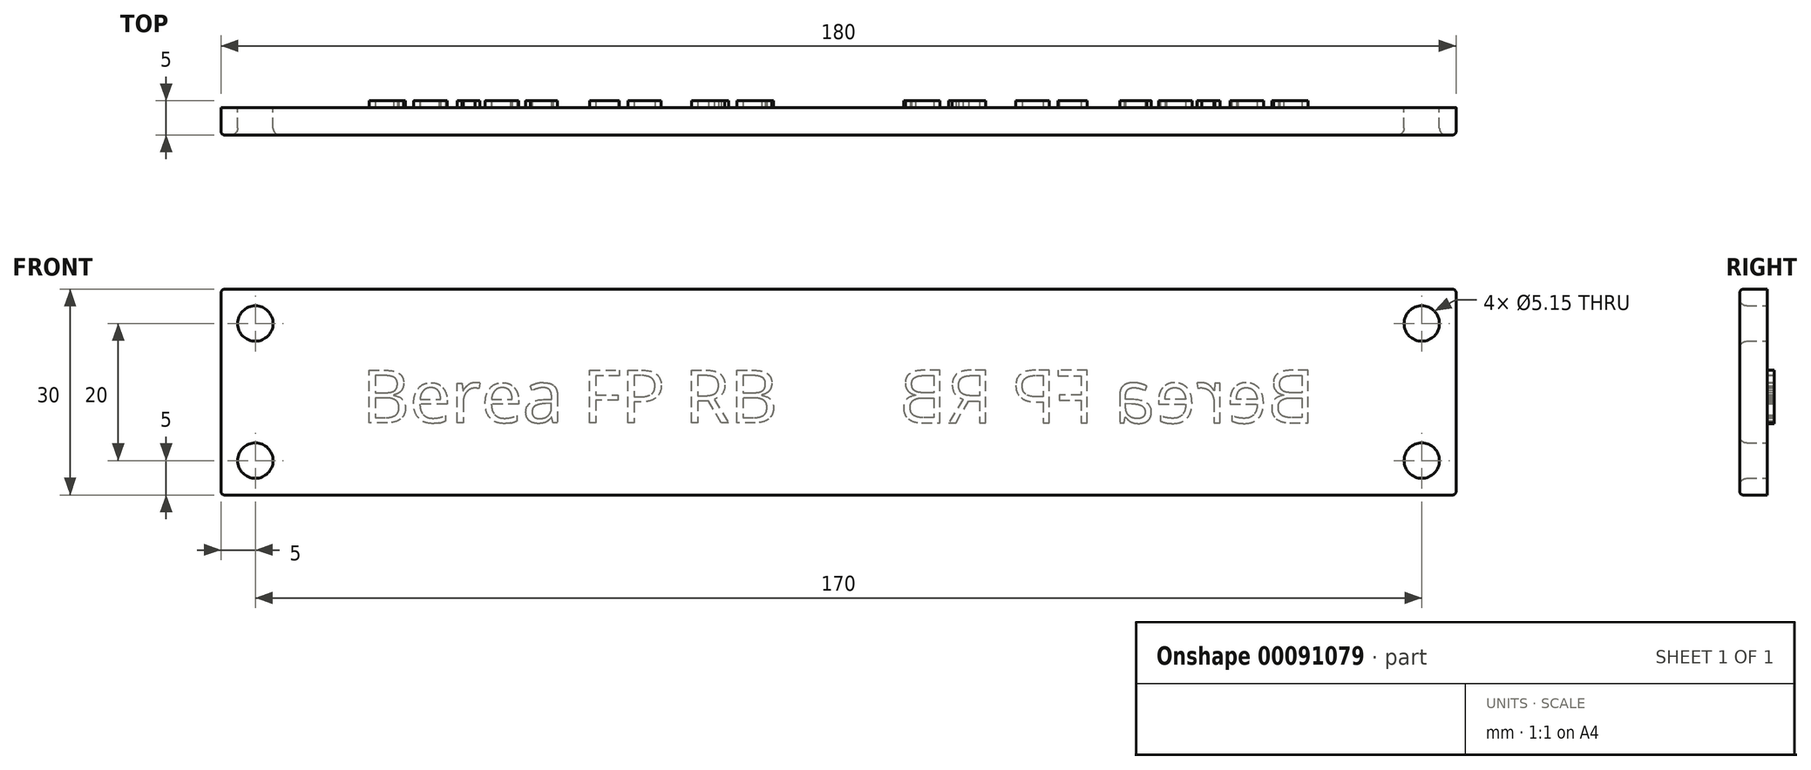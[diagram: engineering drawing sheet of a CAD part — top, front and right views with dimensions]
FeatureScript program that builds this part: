
annotation { "Feature Type Name" : "Feature", "Feature Type Description" : "" }
export const myFeature = defineFeature(function(context is Context, id is Id, definition is map)
    precondition{}
    {
        {
            var Q0;
            Q0=qCreatedBy(makeId("Front.planeOp"),FACE);
            var sketch = newSketch(context, id + "F0", { "sketchPlane" : qUnion([Q0])});
            skLineSegment(sketch, "E0.bottom", {"start": v(-90, -15) * mm, "end": v(90, -15) * mm});
            skLineSegment(sketch, "E0.top", {"start": v(-90, 15) * mm, "end": v(90, 15) * mm});
            skLineSegment(sketch, "E0.left", {"start": v(-90, -15) * mm, "end": v(-90, 15) * mm});
            skLineSegment(sketch, "E0.right", {"start": v(90, -15) * mm, "end": v(90, 15) * mm});
            skPoint(sketch, "E0.middle", {"position": v(0, 0) * mm});
            skCircle(sketch, "E1", {"center": v(-85, 10) * mm, "radius": 2.58 * mm});
            skPoint(sketch, "E2.start.orphan", {"position": v(-90, 0) * mm});
            skPoint(sketch, "E3.orphan", {"position": v(0, 15) * mm});
            skPoint(sketch, "E4.end.orphan", {"position": v(0, -15) * mm});
            skLineSegment(sketch, "E5", {"start": v(-90, 0) * mm, "end": v(0, 0) * mm, "construction": true});
            skLineSegment(sketch, "E6", {"start": v(0, 15) * mm, "end": v(0, -15) * mm, "construction": true});
            skCircle(sketch, "E7.MirrorC", {"center": v(-85, -10) * mm, "radius": 2.58 * mm});
            skCircle(sketch, "E8.MirrorC", {"center": v(85, 10) * mm, "radius": 2.58 * mm});
            skCircle(sketch, "E9.MirrorC", {"center": v(85, -10) * mm, "radius": 2.58 * mm});
            skSolve(sketch);
        }
        {
            var Q0;
            Q0=makeQuery(id+"F0.imprint","IMPRINT",FACE,{"disambiguationData":[TD([[makeQuery(id+"F0.imprint","IMPRINT",EDGE,{"derivedFrom":sQuery(id+"F0.wireOp",EDGE,"E0.bottom")}),1.0]])]});
            extrude(context, id + "F1", {"entities" : qUnion([Q0]), "depth" : 4 * mm});
        }
        {
            var Q0;
            Q0=makeQuery(id+"F1.opExtrude","CAP_EDGE",EDGE,{"disambiguationData":[OSD([sQuery(id+"F0.wireOp",EDGE,"E1")])],"isStart":false});
            var Q1;
            Q1=makeQuery(id+"F1.opExtrude","CAP_EDGE",EDGE,{"disambiguationData":[OSD([sQuery(id+"F0.wireOp",EDGE,"f5b72a5b-8583-449a-bdbf-9ac5a681e1fd0.MirrorC")])],"isStart":false});
            var Q2;
            Q2=makeQuery(id+"F1.opExtrude","CAP_EDGE",EDGE,{"disambiguationData":[OSD([sQuery(id+"F0.wireOp",EDGE,"2623e306-60f4-4522-aa65-1e3e8c2cf5b60.MirrorC")])],"isStart":false});
            var Q3;
            Q3=makeQuery(id+"F1.opExtrude","CAP_EDGE",EDGE,{"disambiguationData":[OSD([sQuery(id+"F0.wireOp",EDGE,"be81a34d-1d50-4ce7-a7a8-4484a1701fac0.MirrorC")])],"isStart":false});
            var Q4;
            Q4=makeQuery(id+"F1.opExtrude","CAP_EDGE",EDGE,{"disambiguationData":[OSD([sQuery(id+"F0.wireOp",EDGE,"E7.MirrorC")])],"isStart":false});
            var Q5;
            Q5=makeQuery(id+"F1.opExtrude","CAP_EDGE",EDGE,{"disambiguationData":[OSD([sQuery(id+"F0.wireOp",EDGE,"E8.MirrorC")])],"isStart":false});
            var Q6;
            Q6=makeQuery(id+"F1.opExtrude","CAP_EDGE",EDGE,{"disambiguationData":[OSD([sQuery(id+"F0.wireOp",EDGE,"E9.MirrorC")])],"isStart":false});
            fillet(context, id + "F2", {"entities" : qUnion([Q0, Q1, Q2, Q3, Q4, Q5, Q6]), "radius" : 1 * mm, "tangentPropagation" : true, "allowEdgeOverflow" : false});
        }
        {
            var Q0;
            Q0=makeQuery(id+"F1.opExtrude","CAP_EDGE",EDGE,{"disambiguationData":[OSD([sQuery(id+"F0.wireOp",EDGE,"E0.top")])],"isStart":false});
            var Q1;
            Q1=makeQuery(id+"F1.opExtrude","CAP_EDGE",EDGE,{"disambiguationData":[OSD([sQuery(id+"F0.wireOp",EDGE,"E0.left")])],"isStart":false});
            var Q2;
            Q2=makeQuery(id+"F1.opExtrude","CAP_EDGE",EDGE,{"disambiguationData":[OSD([sQuery(id+"F0.wireOp",EDGE,"E0.bottom")])],"isStart":false});
            var Q3;
            Q3=makeQuery(id+"F1.opExtrude","CAP_EDGE",EDGE,{"disambiguationData":[OSD([sQuery(id+"F0.wireOp",EDGE,"E0.right")])],"isStart":false});
            var Q4;
            Q4=makeQuery(id+"F1.opExtrude","SWEPT_EDGE",EDGE,{"disambiguationData":[OSD([sQuery(id+"F0.wireOp",EDGE,"E0.top"),sQuery(id+"F0.wireOp",EDGE,"E0.left")])]});
            var Q5;
            Q5=makeQuery(id+"F1.opExtrude","SWEPT_EDGE",EDGE,{"disambiguationData":[OSD([sQuery(id+"F0.wireOp",EDGE,"E0.bottom"),sQuery(id+"F0.wireOp",EDGE,"E0.left")])]});
            var Q6;
            Q6=makeQuery(id+"F1.opExtrude","SWEPT_EDGE",EDGE,{"disambiguationData":[OSD([sQuery(id+"F0.wireOp",EDGE,"E0.top"),sQuery(id+"F0.wireOp",EDGE,"E0.right")])]});
            var Q7;
            Q7=makeQuery(id+"F1.opExtrude","SWEPT_EDGE",EDGE,{"disambiguationData":[OSD([sQuery(id+"F0.wireOp",EDGE,"E0.bottom"),sQuery(id+"F0.wireOp",EDGE,"E0.right")])]});
            fillet(context, id + "F3", {"entities" : qUnion([Q0, Q1, Q2, Q3, Q4, Q5, Q6, Q7]), "radius" : .5 * mm, "tangentPropagation" : true, "allowEdgeOverflow" : false});
        }
        {
            var Q0;
            Q0=makeQuery(id+"F1.opExtrude","CAP_FACE",FACE,{"disambiguationData":[OSD([sQuery(id+"F0.wireOp",EDGE,"E0.bottom"),sQuery(id+"F0.wireOp",EDGE,"E0.top"),sQuery(id+"F0.wireOp",EDGE,"E0.left"),sQuery(id+"F0.wireOp",EDGE,"E0.right"),sQuery(id+"F0.wireOp",EDGE,"E1"),sQuery(id+"F0.wireOp",EDGE,"E7.MirrorC"),sQuery(id+"F0.wireOp",EDGE,"E8.MirrorC"),sQuery(id+"F0.wireOp",EDGE,"E9.MirrorC")])],"isStart":true});
            var sketch = newSketch(context, id + "F4", { "sketchPlane" : qUnion([Q0])});
            skText(sketch, "E10", { "text": "Berea FP RB", "fontName": "OpenSans-Regular.ttf"});
            skLineSegment(sketch, "E11", {"start": v(0, 15) * mm, "end": v(0, -15) * mm, "construction": true});
            const initialGuessF4  = {"E10": [-0.0695, -0.00448, 1, 0, 0.00774]};
            skSetInitialGuess(sketch, initialGuessF4);
            skSolve(sketch);
        }
        {
            var Q0;
            Q0=qSketchRegion(id+"F4",true);
            extrude(context, id + "F5", {"entities" : qUnion([Q0]), "operationType" : NewBodyOperationType.ADD, "depth" : 1 * mm});
        }
        {
            var Q0;
            Q0=makeQuery(id+"F1.opExtrude","SWEPT_BODY",BODY,{"disambiguationData":[OSD([sQuery(id+"F0.wireOp",EDGE,"E0.bottom"),sQuery(id+"F0.wireOp",EDGE,"E0.top"),sQuery(id+"F0.wireOp",EDGE,"E0.left"),sQuery(id+"F0.wireOp",EDGE,"E0.right"),sQuery(id+"F0.wireOp",EDGE,"E1"),sQuery(id+"F0.wireOp",EDGE,"E7.MirrorC"),sQuery(id+"F0.wireOp",EDGE,"E8.MirrorC"),sQuery(id+"F0.wireOp",EDGE,"E9.MirrorC")])]});
            var Q1;
            Q1=makeQuery(id+"F5.opExtrude","SWEPT_FACE",FACE,{"disambiguationData":[OSD([sQuery(id+"F4.wireOp",EDGE,"E10.sketch_text.stroke-94")])]});
            var Q2;
            Q2=makeQuery(id+"F5.opExtrude","SWEPT_FACE",FACE,{"disambiguationData":[OSD([sQuery(id+"F4.wireOp",EDGE,"E10.sketch_text.stroke-169")])]});
            var Q3;
            Q3=makeQuery(id+"F5.opExtrude","SWEPT_FACE",FACE,{"disambiguationData":[OSD([sQuery(id+"F4.wireOp",EDGE,"E10.sketch_text.stroke-185")])]});
            var Q4;
            Q4=makeQuery(id+"F5.opExtrude","SWEPT_FACE",FACE,{"disambiguationData":[OSD([sQuery(id+"F4.wireOp",EDGE,"E10.sketch_text.stroke-125")])]});
            var Q5;
            Q5=makeQuery(id+"F5.opExtrude","SWEPT_FACE",FACE,{"disambiguationData":[OSD([sQuery(id+"F4.wireOp",EDGE,"E10.sketch_text.stroke-155")])]});
            var Q6;
            Q6=makeQuery(id+"F5.opExtrude","SWEPT_FACE",FACE,{"disambiguationData":[OSD([sQuery(id+"F4.wireOp",EDGE,"E10.sketch_text.stroke-65")])]});
            var Q7;
            Q7=makeQuery(id+"F5.opExtrude","SWEPT_FACE",FACE,{"disambiguationData":[OSD([sQuery(id+"F4.wireOp",EDGE,"E10.sketch_text.stroke-81")])]});
            var Q8;
            Q8=makeQuery(id+"F5.opExtrude","SWEPT_FACE",FACE,{"disambiguationData":[OSD([sQuery(id+"F4.wireOp",EDGE,"E10.sketch_text.stroke-67")])]});
            var Q9;
            Q9=makeQuery(id+"F5.opExtrude","SWEPT_FACE",FACE,{"disambiguationData":[OSD([sQuery(id+"F4.wireOp",EDGE,"E10.sketch_text.stroke-99")])]});
            var Q10;
            Q10=makeQuery(id+"F5.opExtrude","SWEPT_FACE",FACE,{"disambiguationData":[OSD([sQuery(id+"F4.wireOp",EDGE,"E10.sketch_text.stroke-127")])]});
            var Q11;
            Q11=makeQuery(id+"F5.opExtrude","SWEPT_FACE",FACE,{"disambiguationData":[OSD([sQuery(id+"F4.wireOp",EDGE,"E10.sketch_text.stroke-10")])]});
            var Q12;
            Q12=makeQuery(id+"F5.opExtrude","CAP_FACE",FACE,{"disambiguationData":[OSD([sQuery(id+"F4.wireOp",EDGE,"E10.sketch_text.stroke-9"),sQuery(id+"F4.wireOp",EDGE,"E10.sketch_text.stroke-10"),sQuery(id+"F4.wireOp",EDGE,"E10.sketch_text.stroke-11"),sQuery(id+"F4.wireOp",EDGE,"E10.sketch_text.stroke-12")])],"isStart":false});
            var Q13;
            Q13=makeQuery(id+"F5.opExtrude","SWEPT_FACE",FACE,{"disambiguationData":[OSD([sQuery(id+"F4.wireOp",EDGE,"E10.sketch_text.stroke-154")])]});
            var Q14;
            Q14=makeQuery(id+"F5.opExtrude","SWEPT_FACE",FACE,{"disambiguationData":[OSD([sQuery(id+"F4.wireOp",EDGE,"E10.sketch_text.stroke-1")])]});
            var Q15;
            Q15=makeQuery(id+"F5.opExtrude","CAP_FACE",FACE,{"disambiguationData":[OSD([sQuery(id+"F4.wireOp",EDGE,"E10.sketch_text.stroke-124"),sQuery(id+"F4.wireOp",EDGE,"E10.sketch_text.stroke-125"),sQuery(id+"F4.wireOp",EDGE,"E10.sketch_text.stroke-126"),sQuery(id+"F4.wireOp",EDGE,"E10.sketch_text.stroke-127"),sQuery(id+"F4.wireOp",EDGE,"E10.sketch_text.stroke-128"),sQuery(id+"F4.wireOp",EDGE,"E10.sketch_text.stroke-129"),sQuery(id+"F4.wireOp",EDGE,"E10.sketch_text.stroke-130"),sQuery(id+"F4.wireOp",EDGE,"E10.sketch_text.stroke-131"),sQuery(id+"F4.wireOp",EDGE,"E10.sketch_text.stroke-132"),sQuery(id+"F4.wireOp",EDGE,"E10.sketch_text.stroke-133"),sQuery(id+"F4.wireOp",EDGE,"E10.sketch_text.stroke-134"),sQuery(id+"F4.wireOp",EDGE,"E10.sketch_text.stroke-135"),sQuery(id+"F4.wireOp",EDGE,"E10.sketch_text.stroke-136"),sQuery(id+"F4.wireOp",EDGE,"E10.sketch_text.stroke-137"),sQuery(id+"F4.wireOp",EDGE,"E10.sketch_text.stroke-138")])],"isStart":false});
            var Q16;
            Q16=makeQuery(id+"F5.opExtrude","CAP_FACE",FACE,{"disambiguationData":[OSD([sQuery(id+"F4.wireOp",EDGE,"E10.sketch_text.stroke-34"),sQuery(id+"F4.wireOp",EDGE,"E10.sketch_text.stroke-35"),sQuery(id+"F4.wireOp",EDGE,"E10.sketch_text.stroke-36"),sQuery(id+"F4.wireOp",EDGE,"E10.sketch_text.stroke-37"),sQuery(id+"F4.wireOp",EDGE,"E10.sketch_text.stroke-38"),sQuery(id+"F4.wireOp",EDGE,"E10.sketch_text.stroke-39"),sQuery(id+"F4.wireOp",EDGE,"E10.sketch_text.stroke-40"),sQuery(id+"F4.wireOp",EDGE,"E10.sketch_text.stroke-41"),sQuery(id+"F4.wireOp",EDGE,"E10.sketch_text.stroke-42"),sQuery(id+"F4.wireOp",EDGE,"E10.sketch_text.stroke-43"),sQuery(id+"F4.wireOp",EDGE,"E10.sketch_text.stroke-44"),sQuery(id+"F4.wireOp",EDGE,"E10.sketch_text.stroke-45"),sQuery(id+"F4.wireOp",EDGE,"E10.sketch_text.stroke-46"),sQuery(id+"F4.wireOp",EDGE,"E10.sketch_text.stroke-47"),sQuery(id+"F4.wireOp",EDGE,"E10.sketch_text.stroke-48"),sQuery(id+"F4.wireOp",EDGE,"E10.sketch_text.stroke-49"),sQuery(id+"F4.wireOp",EDGE,"E10.sketch_text.stroke-50"),sQuery(id+"F4.wireOp",EDGE,"E10.sketch_text.stroke-51"),sQuery(id+"F4.wireOp",EDGE,"E10.sketch_text.stroke-52"),sQuery(id+"F4.wireOp",EDGE,"E10.sketch_text.stroke-53"),sQuery(id+"F4.wireOp",EDGE,"E10.sketch_text.stroke-54"),sQuery(id+"F4.wireOp",EDGE,"E10.sketch_text.stroke-55"),sQuery(id+"F4.wireOp",EDGE,"E10.sketch_text.stroke-56"),sQuery(id+"F4.wireOp",EDGE,"E10.sketch_text.stroke-57"),sQuery(id+"F4.wireOp",EDGE,"E10.sketch_text.stroke-58"),sQuery(id+"F4.wireOp",EDGE,"E10.sketch_text.stroke-59"),sQuery(id+"F4.wireOp",EDGE,"E10.sketch_text.stroke-60")])],"isStart":false});
            var Q17;
            Q17=makeQuery(id+"F5.opExtrude","SWEPT_FACE",FACE,{"disambiguationData":[OSD([sQuery(id+"F4.wireOp",EDGE,"E10.sketch_text.stroke-50")])]});
            var Q18;
            Q18=makeQuery(id+"F5.opExtrude","SWEPT_FACE",FACE,{"disambiguationData":[OSD([sQuery(id+"F4.wireOp",EDGE,"E10.sketch_text.stroke-2")])]});
            var Q19;
            Q19=makeQuery(id+"F5.opExtrude","SWEPT_FACE",FACE,{"disambiguationData":[OSD([sQuery(id+"F4.wireOp",EDGE,"E10.sketch_text.stroke-3")])]});
            var Q20;
            Q20=makeQuery(id+"F5.opExtrude","SWEPT_FACE",FACE,{"disambiguationData":[OSD([sQuery(id+"F4.wireOp",EDGE,"E10.sketch_text.stroke-5")])]});
            var Q21;
            Q21=makeQuery(id+"F5.opExtrude","SWEPT_FACE",FACE,{"disambiguationData":[OSD([sQuery(id+"F4.wireOp",EDGE,"E10.sketch_text.stroke-8")])]});
            var Q22;
            Q22=makeQuery(id+"F5.opExtrude","SWEPT_FACE",FACE,{"disambiguationData":[OSD([sQuery(id+"F4.wireOp",EDGE,"E10.sketch_text.stroke-98")])]});
            var Q23;
            Q23=makeQuery(id+"F5.opExtrude","SWEPT_FACE",FACE,{"disambiguationData":[OSD([sQuery(id+"F4.wireOp",EDGE,"E10.sketch_text.stroke-66")])]});
            var Q24;
            Q24=makeQuery(id+"F5.opExtrude","SWEPT_FACE",FACE,{"disambiguationData":[OSD([sQuery(id+"F4.wireOp",EDGE,"E10.sketch_text.stroke-153")])]});
            var Q25;
            Q25=makeQuery(id+"F5.opExtrude","SWEPT_FACE",FACE,{"disambiguationData":[OSD([sQuery(id+"F4.wireOp",EDGE,"E10.sketch_text.stroke-126")])]});
            var Q26;
            Q26=makeQuery(id+"F5.opExtrude","SWEPT_FACE",FACE,{"disambiguationData":[OSD([sQuery(id+"F4.wireOp",EDGE,"E10.sketch_text.stroke-183")])]});
            var Q27;
            Q27=makeQuery(id+"F5.opExtrude","SWEPT_FACE",FACE,{"disambiguationData":[OSD([sQuery(id+"F4.wireOp",EDGE,"E10.sketch_text.stroke-109")])]});
            var Q28;
            Q28=makeQuery(id+"F5.opExtrude","SWEPT_FACE",FACE,{"disambiguationData":[OSD([sQuery(id+"F4.wireOp",EDGE,"E10.sketch_text.stroke-186")])]});
            var Q29;
            Q29=makeQuery(id+"F5.opExtrude","SWEPT_FACE",FACE,{"disambiguationData":[OSD([sQuery(id+"F4.wireOp",EDGE,"E10.sketch_text.stroke-79")])]});
            var Q30;
            Q30=makeQuery(id+"F5.opExtrude","SWEPT_FACE",FACE,{"disambiguationData":[OSD([sQuery(id+"F4.wireOp",EDGE,"E10.sketch_text.stroke-110")])]});
            var Q31;
            Q31=makeQuery(id+"F5.opExtrude","SWEPT_FACE",FACE,{"disambiguationData":[OSD([sQuery(id+"F4.wireOp",EDGE,"E10.sketch_text.stroke-38")])]});
            var Q32;
            Q32=makeQuery(id+"F5.opExtrude","SWEPT_FACE",FACE,{"disambiguationData":[OSD([sQuery(id+"F4.wireOp",EDGE,"E10.sketch_text.stroke-24")])]});
            var Q33;
            Q33=makeQuery(id+"F5.opExtrude","SWEPT_FACE",FACE,{"disambiguationData":[OSD([sQuery(id+"F4.wireOp",EDGE,"E10.sketch_text.stroke-12")])]});
            var Q34;
            Q34=makeQuery(id+"F5.opExtrude","SWEPT_FACE",FACE,{"disambiguationData":[OSD([sQuery(id+"F4.wireOp",EDGE,"E10.sketch_text.stroke-100")])]});
            var Q35;
            Q35=makeQuery(id+"F5.opExtrude","SWEPT_FACE",FACE,{"disambiguationData":[OSD([sQuery(id+"F4.wireOp",EDGE,"E10.sketch_text.stroke-158")])]});
            var Q36;
            Q36=makeQuery(id+"F5.opExtrude","SWEPT_FACE",FACE,{"disambiguationData":[OSD([sQuery(id+"F4.wireOp",EDGE,"E10.sketch_text.stroke-142")])]});
            var Q37;
            Q37=makeQuery(id+"F5.opExtrude","SWEPT_FACE",FACE,{"disambiguationData":[OSD([sQuery(id+"F4.wireOp",EDGE,"E10.sketch_text.stroke-54")])]});
            var Q38;
            Q38=makeQuery(id+"F5.opExtrude","SWEPT_FACE",FACE,{"disambiguationData":[OSD([sQuery(id+"F4.wireOp",EDGE,"E10.sketch_text.stroke-25")])]});
            var Q39;
            Q39=makeQuery(id+"F5.opExtrude","SWEPT_FACE",FACE,{"disambiguationData":[OSD([sQuery(id+"F4.wireOp",EDGE,"E10.sketch_text.stroke-101")])]});
            var Q40;
            Q40=makeQuery(id+"F5.opExtrude","SWEPT_FACE",FACE,{"disambiguationData":[OSD([sQuery(id+"F4.wireOp",EDGE,"E10.sketch_text.stroke-69")])]});
            var Q41;
            Q41=makeQuery(id+"F5.opExtrude","SWEPT_FACE",FACE,{"disambiguationData":[OSD([sQuery(id+"F4.wireOp",EDGE,"E10.sketch_text.stroke-159")])]});
            var Q42;
            Q42=makeQuery(id+"F5.opExtrude","SWEPT_FACE",FACE,{"disambiguationData":[OSD([sQuery(id+"F4.wireOp",EDGE,"E10.sketch_text.stroke-85")])]});
            var Q43;
            Q43=makeQuery(id+"F5.opExtrude","SWEPT_FACE",FACE,{"disambiguationData":[OSD([sQuery(id+"F4.wireOp",EDGE,"E10.sketch_text.stroke-173")])]});
            var Q44;
            Q44=makeQuery(id+"F5.opExtrude","SWEPT_FACE",FACE,{"disambiguationData":[OSD([sQuery(id+"F4.wireOp",EDGE,"E10.sketch_text.stroke-40")])]});
            var Q45;
            Q45=makeQuery(id+"F5.opExtrude","SWEPT_FACE",FACE,{"disambiguationData":[OSD([sQuery(id+"F4.wireOp",EDGE,"E10.sketch_text.stroke-102")])]});
            var Q46;
            Q46=makeQuery(id+"F5.opExtrude","SWEPT_FACE",FACE,{"disambiguationData":[OSD([sQuery(id+"F4.wireOp",EDGE,"E10.sketch_text.stroke-86")])]});
            var Q47;
            Q47=makeQuery(id+"F5.opExtrude","SWEPT_FACE",FACE,{"disambiguationData":[OSD([sQuery(id+"F4.wireOp",EDGE,"E10.sketch_text.stroke-130")])]});
            var Q48;
            Q48=makeQuery(id+"F5.opExtrude","SWEPT_FACE",FACE,{"disambiguationData":[OSD([sQuery(id+"F4.wireOp",EDGE,"E10.sketch_text.stroke-103")])]});
            var Q49;
            Q49=makeQuery(id+"F5.opExtrude","SWEPT_FACE",FACE,{"disambiguationData":[OSD([sQuery(id+"F4.wireOp",EDGE,"E10.sketch_text.stroke-87")])]});
            var Q50;
            Q50=makeQuery(id+"F5.opExtrude","SWEPT_FACE",FACE,{"disambiguationData":[OSD([sQuery(id+"F4.wireOp",EDGE,"E10.sketch_text.stroke-145")])]});
            var Q51;
            Q51=makeQuery(id+"F5.opExtrude","SWEPT_FACE",FACE,{"disambiguationData":[OSD([sQuery(id+"F4.wireOp",EDGE,"E10.sketch_text.stroke-131")])]});
            var Q52;
            Q52=makeQuery(id+"F5.opExtrude","SWEPT_FACE",FACE,{"disambiguationData":[OSD([sQuery(id+"F4.wireOp",EDGE,"E10.sketch_text.stroke-28")])]});
            var Q53;
            Q53=makeQuery(id+"F5.opExtrude","SWEPT_FACE",FACE,{"disambiguationData":[OSD([sQuery(id+"F4.wireOp",EDGE,"E10.sketch_text.stroke-14")])]});
            var Q54;
            Q54=makeQuery(id+"F5.opExtrude","SWEPT_FACE",FACE,{"disambiguationData":[OSD([sQuery(id+"F4.wireOp",EDGE,"E10.sketch_text.stroke-88")])]});
            var Q55;
            Q55=makeQuery(id+"F5.opExtrude","SWEPT_FACE",FACE,{"disambiguationData":[OSD([sQuery(id+"F4.wireOp",EDGE,"E10.sketch_text.stroke-162")])]});
            var Q56;
            Q56=makeQuery(id+"F5.opExtrude","SWEPT_FACE",FACE,{"disambiguationData":[OSD([sQuery(id+"F4.wireOp",EDGE,"E10.sketch_text.stroke-176")])]});
            var Q57;
            Q57=makeQuery(id+"F5.opExtrude","SWEPT_FACE",FACE,{"disambiguationData":[OSD([sQuery(id+"F4.wireOp",EDGE,"E10.sketch_text.stroke-73")])]});
            var Q58;
            Q58=makeQuery(id+"F5.opExtrude","SWEPT_FACE",FACE,{"disambiguationData":[OSD([sQuery(id+"F4.wireOp",EDGE,"E10.sketch_text.stroke-59")])]});
            var Q59;
            Q59=makeQuery(id+"F5.opExtrude","SWEPT_FACE",FACE,{"disambiguationData":[OSD([sQuery(id+"F4.wireOp",EDGE,"E10.sketch_text.stroke-133")])]});
            var Q60;
            Q60=makeQuery(id+"F5.opExtrude","SWEPT_FACE",FACE,{"disambiguationData":[OSD([sQuery(id+"F4.wireOp",EDGE,"E10.sketch_text.stroke-119")])]});
            var Q61;
            Q61=makeQuery(id+"F5.opExtrude","SWEPT_FACE",FACE,{"disambiguationData":[OSD([sQuery(id+"F4.wireOp",EDGE,"E10.sketch_text.stroke-74")])]});
            var Q62;
            Q62=makeQuery(id+"F5.opExtrude","SWEPT_FACE",FACE,{"disambiguationData":[OSD([sQuery(id+"F4.wireOp",EDGE,"E10.sketch_text.stroke-44")])]});
            var Q63;
            Q63=makeQuery(id+"F5.opExtrude","SWEPT_FACE",FACE,{"disambiguationData":[OSD([sQuery(id+"F4.wireOp",EDGE,"E10.sketch_text.stroke-120")])]});
            var Q64;
            Q64=makeQuery(id+"F5.opExtrude","SWEPT_FACE",FACE,{"disambiguationData":[OSD([sQuery(id+"F4.wireOp",EDGE,"E10.sketch_text.stroke-90")])]});
            var Q65;
            Q65=makeQuery(id+"F5.opExtrude","SWEPT_FACE",FACE,{"disambiguationData":[OSD([sQuery(id+"F4.wireOp",EDGE,"E10.sketch_text.stroke-178")])]});
            var Q66;
            Q66=makeQuery(id+"F5.opExtrude","SWEPT_FACE",FACE,{"disambiguationData":[OSD([sQuery(id+"F4.wireOp",EDGE,"E10.sketch_text.stroke-45")])]});
            var Q67;
            Q67=makeQuery(id+"F5.opExtrude","SWEPT_FACE",FACE,{"disambiguationData":[OSD([sQuery(id+"F4.wireOp",EDGE,"E10.sketch_text.stroke-31")])]});
            var Q68;
            Q68=makeQuery(id+"F5.opExtrude","SWEPT_FACE",FACE,{"disambiguationData":[OSD([sQuery(id+"F4.wireOp",EDGE,"E10.sketch_text.stroke-135")])]});
            var Q69;
            Q69=makeQuery(id+"F5.opExtrude","SWEPT_FACE",FACE,{"disambiguationData":[OSD([sQuery(id+"F4.wireOp",EDGE,"E10.sketch_text.stroke-179")])]});
            var Q70;
            Q70=makeQuery(id+"F5.opExtrude","SWEPT_FACE",FACE,{"disambiguationData":[OSD([sQuery(id+"F4.wireOp",EDGE,"E10.sketch_text.stroke-165")])]});
            var Q71;
            Q71=makeQuery(id+"F5.opExtrude","SWEPT_FACE",FACE,{"disambiguationData":[OSD([sQuery(id+"F4.wireOp",EDGE,"E10.sketch_text.stroke-149")])]});
            var Q72;
            Q72=makeQuery(id+"F5.opExtrude","SWEPT_FACE",FACE,{"disambiguationData":[OSD([sQuery(id+"F4.wireOp",EDGE,"E10.sketch_text.stroke-136")])]});
            var Q73;
            Q73=makeQuery(id+"F5.opExtrude","SWEPT_FACE",FACE,{"disambiguationData":[OSD([sQuery(id+"F4.wireOp",EDGE,"E10.sketch_text.stroke-122")])]});
            var Q74;
            Q74=makeQuery(id+"F5.opExtrude","SWEPT_FACE",FACE,{"disambiguationData":[OSD([sQuery(id+"F4.wireOp",EDGE,"E10.sketch_text.stroke-106")])]});
            var Q75;
            Q75=makeQuery(id+"F5.opExtrude","SWEPT_FACE",FACE,{"disambiguationData":[OSD([sQuery(id+"F4.wireOp",EDGE,"E10.sketch_text.stroke-180")])]});
            var Q76;
            Q76=makeQuery(id+"F5.opExtrude","SWEPT_FACE",FACE,{"disambiguationData":[OSD([sQuery(id+"F4.wireOp",EDGE,"E10.sketch_text.stroke-166")])]});
            var Q77;
            Q77=makeQuery(id+"F5.opExtrude","SWEPT_FACE",FACE,{"disambiguationData":[OSD([sQuery(id+"F4.wireOp",EDGE,"E10.sketch_text.stroke-150")])]});
            var Q78;
            Q78=makeQuery(id+"F5.opExtrude","SWEPT_FACE",FACE,{"disambiguationData":[OSD([sQuery(id+"F4.wireOp",EDGE,"E10.sketch_text.stroke-76")])]});
            var Q79;
            Q79=makeQuery(id+"F5.opExtrude","SWEPT_FACE",FACE,{"disambiguationData":[OSD([sQuery(id+"F4.wireOp",EDGE,"E10.sketch_text.stroke-32")])]});
            var Q80;
            Q80=makeQuery(id+"F5.opExtrude","SWEPT_FACE",FACE,{"disambiguationData":[OSD([sQuery(id+"F4.wireOp",EDGE,"E10.sketch_text.stroke-181")])]});
            var Q81;
            Q81=makeQuery(id+"F5.opExtrude","SWEPT_FACE",FACE,{"disambiguationData":[OSD([sQuery(id+"F4.wireOp",EDGE,"E10.sketch_text.stroke-47")])]});
            var Q82;
            Q82=makeQuery(id+"F5.opExtrude","SWEPT_FACE",FACE,{"disambiguationData":[OSD([sQuery(id+"F4.wireOp",EDGE,"E10.sketch_text.stroke-123")])]});
            var Q83;
            Q83=makeQuery(id+"F5.opExtrude","SWEPT_FACE",FACE,{"disambiguationData":[OSD([sQuery(id+"F4.wireOp",EDGE,"E10.sketch_text.stroke-107")])]});
            var Q84;
            Q84=makeQuery(id+"F5.opExtrude","SWEPT_FACE",FACE,{"disambiguationData":[OSD([sQuery(id+"F4.wireOp",EDGE,"E10.sketch_text.stroke-48")])]});
            var Q85;
            Q85=makeQuery(id+"F5.opExtrude","SWEPT_FACE",FACE,{"disambiguationData":[OSD([sQuery(id+"F4.wireOp",EDGE,"E10.sketch_text.stroke-124")])]});
            var Q86;
            Q86=makeQuery(id+"F5.opExtrude","SWEPT_FACE",FACE,{"disambiguationData":[OSD([sQuery(id+"F4.wireOp",EDGE,"E10.sketch_text.stroke-108")])]});
            var Q87;
            Q87=makeQuery(id+"F5.opExtrude","CAP_FACE",FACE,{"disambiguationData":[OSD([sQuery(id+"F4.wireOp",EDGE,"E10.sketch_text.stroke-139"),sQuery(id+"F4.wireOp",EDGE,"E10.sketch_text.stroke-140"),sQuery(id+"F4.wireOp",EDGE,"E10.sketch_text.stroke-141"),sQuery(id+"F4.wireOp",EDGE,"E10.sketch_text.stroke-142"),sQuery(id+"F4.wireOp",EDGE,"E10.sketch_text.stroke-143"),sQuery(id+"F4.wireOp",EDGE,"E10.sketch_text.stroke-144"),sQuery(id+"F4.wireOp",EDGE,"E10.sketch_text.stroke-145"),sQuery(id+"F4.wireOp",EDGE,"E10.sketch_text.stroke-146"),sQuery(id+"F4.wireOp",EDGE,"E10.sketch_text.stroke-147"),sQuery(id+"F4.wireOp",EDGE,"E10.sketch_text.stroke-148"),sQuery(id+"F4.wireOp",EDGE,"E10.sketch_text.stroke-149"),sQuery(id+"F4.wireOp",EDGE,"E10.sketch_text.stroke-150"),sQuery(id+"F4.wireOp",EDGE,"E10.sketch_text.stroke-151"),sQuery(id+"F4.wireOp",EDGE,"E10.sketch_text.stroke-152"),sQuery(id+"F4.wireOp",EDGE,"E10.sketch_text.stroke-153"),sQuery(id+"F4.wireOp",EDGE,"E10.sketch_text.stroke-154"),sQuery(id+"F4.wireOp",EDGE,"E10.sketch_text.stroke-155"),sQuery(id+"F4.wireOp",EDGE,"E10.sketch_text.stroke-156"),sQuery(id+"F4.wireOp",EDGE,"E10.sketch_text.stroke-157"),sQuery(id+"F4.wireOp",EDGE,"E10.sketch_text.stroke-158"),sQuery(id+"F4.wireOp",EDGE,"E10.sketch_text.stroke-159"),sQuery(id+"F4.wireOp",EDGE,"E10.sketch_text.stroke-160"),sQuery(id+"F4.wireOp",EDGE,"E10.sketch_text.stroke-161"),sQuery(id+"F4.wireOp",EDGE,"E10.sketch_text.stroke-162"),sQuery(id+"F4.wireOp",EDGE,"E10.sketch_text.stroke-163"),sQuery(id+"F4.wireOp",EDGE,"E10.sketch_text.stroke-164"),sQuery(id+"F4.wireOp",EDGE,"E10.sketch_text.stroke-165")])],"isStart":false});
            var Q88;
            Q88=makeQuery(id+"F5.opExtrude","CAP_FACE",FACE,{"disambiguationData":[OSD([sQuery(id+"F4.wireOp",EDGE,"E10.sketch_text.stroke-21"),sQuery(id+"F4.wireOp",EDGE,"E10.sketch_text.stroke-22"),sQuery(id+"F4.wireOp",EDGE,"E10.sketch_text.stroke-23"),sQuery(id+"F4.wireOp",EDGE,"E10.sketch_text.stroke-24"),sQuery(id+"F4.wireOp",EDGE,"E10.sketch_text.stroke-25"),sQuery(id+"F4.wireOp",EDGE,"E10.sketch_text.stroke-26"),sQuery(id+"F4.wireOp",EDGE,"E10.sketch_text.stroke-27"),sQuery(id+"F4.wireOp",EDGE,"E10.sketch_text.stroke-28"),sQuery(id+"F4.wireOp",EDGE,"E10.sketch_text.stroke-29"),sQuery(id+"F4.wireOp",EDGE,"E10.sketch_text.stroke-30"),sQuery(id+"F4.wireOp",EDGE,"E10.sketch_text.stroke-31"),sQuery(id+"F4.wireOp",EDGE,"E10.sketch_text.stroke-32"),sQuery(id+"F4.wireOp",EDGE,"E10.sketch_text.stroke-33")])],"isStart":false});
            var Q89;
            Q89=makeQuery(id+"F5.opExtrude","SWEPT_FACE",FACE,{"disambiguationData":[OSD([sQuery(id+"F4.wireOp",EDGE,"E10.sketch_text.stroke-113")])]});
            var Q90;
            Q90=makeQuery(id+"F5.opExtrude","SWEPT_FACE",FACE,{"disambiguationData":[OSD([sQuery(id+"F4.wireOp",EDGE,"E10.sketch_text.stroke-37")])]});
            var Q91;
            Q91=makeQuery(id+"F5.opExtrude","SWEPT_FACE",FACE,{"disambiguationData":[OSD([sQuery(id+"F4.wireOp",EDGE,"E10.sketch_text.stroke-187")])]});
            var Q92;
            Q92=makeQuery(id+"F5.opExtrude","SWEPT_FACE",FACE,{"disambiguationData":[OSD([sQuery(id+"F4.wireOp",EDGE,"E10.sketch_text.stroke-0")])]});
            var Q93;
            Q93=makeQuery(id+"F5.opExtrude","SWEPT_FACE",FACE,{"disambiguationData":[OSD([sQuery(id+"F4.wireOp",EDGE,"E10.sketch_text.stroke-4")])]});
            var Q94;
            Q94=makeQuery(id+"F5.opExtrude","SWEPT_FACE",FACE,{"disambiguationData":[OSD([sQuery(id+"F4.wireOp",EDGE,"E10.sketch_text.stroke-82")])]});
            var Q95;
            Q95=makeQuery(id+"F5.opExtrude","SWEPT_FACE",FACE,{"disambiguationData":[OSD([sQuery(id+"F4.wireOp",EDGE,"E10.sketch_text.stroke-52")])]});
            var Q96;
            Q96=makeQuery(id+"F5.opExtrude","SWEPT_FACE",FACE,{"disambiguationData":[OSD([sQuery(id+"F4.wireOp",EDGE,"E10.sketch_text.stroke-49")])]});
            var Q97;
            Q97=makeQuery(id+"F5.opExtrude","SWEPT_FACE",FACE,{"disambiguationData":[OSD([sQuery(id+"F4.wireOp",EDGE,"E10.sketch_text.stroke-63")])]});
            var Q98;
            Q98=makeQuery(id+"F5.opExtrude","SWEPT_FACE",FACE,{"disambiguationData":[OSD([sQuery(id+"F4.wireOp",EDGE,"E10.sketch_text.stroke-21")])]});
            var Q99;
            Q99=makeQuery(id+"F5.opExtrude","SWEPT_FACE",FACE,{"disambiguationData":[OSD([sQuery(id+"F4.wireOp",EDGE,"E10.sketch_text.stroke-128")])]});
            var Q100;
            Q100=makeQuery(id+"F5.opExtrude","SWEPT_FACE",FACE,{"disambiguationData":[OSD([sQuery(id+"F4.wireOp",EDGE,"E10.sketch_text.stroke-55")])]});
            var Q101;
            Q101=makeQuery(id+"F5.opExtrude","SWEPT_FACE",FACE,{"disambiguationData":[OSD([sQuery(id+"F4.wireOp",EDGE,"E10.sketch_text.stroke-26")])]});
            var Q102;
            Q102=makeQuery(id+"F5.opExtrude","SWEPT_FACE",FACE,{"disambiguationData":[OSD([sQuery(id+"F4.wireOp",EDGE,"E10.sketch_text.stroke-174")])]});
            var Q103;
            Q103=makeQuery(id+"F5.opExtrude","SWEPT_FACE",FACE,{"disambiguationData":[OSD([sQuery(id+"F4.wireOp",EDGE,"E10.sketch_text.stroke-104")])]});
            var Q104;
            Q104=makeQuery(id+"F5.opExtrude","SWEPT_FACE",FACE,{"disambiguationData":[OSD([sQuery(id+"F4.wireOp",EDGE,"E10.sketch_text.stroke-72")])]});
            var Q105;
            Q105=makeQuery(id+"F5.opExtrude","SWEPT_FACE",FACE,{"disambiguationData":[OSD([sQuery(id+"F4.wireOp",EDGE,"E10.sketch_text.stroke-132")])]});
            var Q106;
            Q106=makeQuery(id+"F5.opExtrude","SWEPT_FACE",FACE,{"disambiguationData":[OSD([sQuery(id+"F4.wireOp",EDGE,"E10.sketch_text.stroke-43")])]});
            var Q107;
            Q107=makeQuery(id+"F5.opExtrude","SWEPT_FACE",FACE,{"disambiguationData":[OSD([sQuery(id+"F4.wireOp",EDGE,"E10.sketch_text.stroke-15")])]});
            var Q108;
            Q108=makeQuery(id+"F5.opExtrude","SWEPT_FACE",FACE,{"disambiguationData":[OSD([sQuery(id+"F4.wireOp",EDGE,"E10.sketch_text.stroke-89")])]});
            var Q109;
            Q109=makeQuery(id+"F5.opExtrude","SWEPT_FACE",FACE,{"disambiguationData":[OSD([sQuery(id+"F4.wireOp",EDGE,"E10.sketch_text.stroke-163")])]});
            var Q110;
            Q110=makeQuery(id+"F5.opExtrude","SWEPT_FACE",FACE,{"disambiguationData":[OSD([sQuery(id+"F4.wireOp",EDGE,"E10.sketch_text.stroke-30")])]});
            var Q111;
            Q111=makeQuery(id+"F5.opExtrude","SWEPT_FACE",FACE,{"disambiguationData":[OSD([sQuery(id+"F4.wireOp",EDGE,"E10.sketch_text.stroke-134")])]});
            var Q112;
            Q112=makeQuery(id+"F5.opExtrude","SWEPT_FACE",FACE,{"disambiguationData":[OSD([sQuery(id+"F4.wireOp",EDGE,"E10.sketch_text.stroke-121")])]});
            var Q113;
            Q113=makeQuery(id+"F5.opExtrude","CAP_FACE",FACE,{"disambiguationData":[OSD([sQuery(id+"F4.wireOp",EDGE,"E10.sketch_text.stroke-105"),sQuery(id+"F4.wireOp",EDGE,"E10.sketch_text.stroke-106"),sQuery(id+"F4.wireOp",EDGE,"E10.sketch_text.stroke-107"),sQuery(id+"F4.wireOp",EDGE,"E10.sketch_text.stroke-108"),sQuery(id+"F4.wireOp",EDGE,"E10.sketch_text.stroke-109"),sQuery(id+"F4.wireOp",EDGE,"E10.sketch_text.stroke-110"),sQuery(id+"F4.wireOp",EDGE,"E10.sketch_text.stroke-111"),sQuery(id+"F4.wireOp",EDGE,"E10.sketch_text.stroke-112"),sQuery(id+"F4.wireOp",EDGE,"E10.sketch_text.stroke-113"),sQuery(id+"F4.wireOp",EDGE,"E10.sketch_text.stroke-114"),sQuery(id+"F4.wireOp",EDGE,"E10.sketch_text.stroke-115"),sQuery(id+"F4.wireOp",EDGE,"E10.sketch_text.stroke-116"),sQuery(id+"F4.wireOp",EDGE,"E10.sketch_text.stroke-117"),sQuery(id+"F4.wireOp",EDGE,"E10.sketch_text.stroke-118"),sQuery(id+"F4.wireOp",EDGE,"E10.sketch_text.stroke-119"),sQuery(id+"F4.wireOp",EDGE,"E10.sketch_text.stroke-120"),sQuery(id+"F4.wireOp",EDGE,"E10.sketch_text.stroke-121"),sQuery(id+"F4.wireOp",EDGE,"E10.sketch_text.stroke-122"),sQuery(id+"F4.wireOp",EDGE,"E10.sketch_text.stroke-123")])],"isStart":false});
            var Q114;
            Q114=makeQuery(id+"F5.opExtrude","SWEPT_FACE",FACE,{"disambiguationData":[OSD([sQuery(id+"F4.wireOp",EDGE,"E10.sketch_text.stroke-92")])]});
            var Q115;
            Q115=makeQuery(id+"F5.opExtrude","SWEPT_FACE",FACE,{"disambiguationData":[OSD([sQuery(id+"F4.wireOp",EDGE,"E10.sketch_text.stroke-46")])]});
            var Q116;
            Q116=makeQuery(id+"F5.opExtrude","CAP_FACE",FACE,{"disambiguationData":[OSD([sQuery(id+"F4.wireOp",EDGE,"E10.sketch_text.stroke-61"),sQuery(id+"F4.wireOp",EDGE,"E10.sketch_text.stroke-62"),sQuery(id+"F4.wireOp",EDGE,"E10.sketch_text.stroke-63"),sQuery(id+"F4.wireOp",EDGE,"E10.sketch_text.stroke-64"),sQuery(id+"F4.wireOp",EDGE,"E10.sketch_text.stroke-65"),sQuery(id+"F4.wireOp",EDGE,"E10.sketch_text.stroke-66"),sQuery(id+"F4.wireOp",EDGE,"E10.sketch_text.stroke-67"),sQuery(id+"F4.wireOp",EDGE,"E10.sketch_text.stroke-68"),sQuery(id+"F4.wireOp",EDGE,"E10.sketch_text.stroke-69"),sQuery(id+"F4.wireOp",EDGE,"E10.sketch_text.stroke-70"),sQuery(id+"F4.wireOp",EDGE,"E10.sketch_text.stroke-71"),sQuery(id+"F4.wireOp",EDGE,"E10.sketch_text.stroke-72"),sQuery(id+"F4.wireOp",EDGE,"E10.sketch_text.stroke-73"),sQuery(id+"F4.wireOp",EDGE,"E10.sketch_text.stroke-74"),sQuery(id+"F4.wireOp",EDGE,"E10.sketch_text.stroke-75"),sQuery(id+"F4.wireOp",EDGE,"E10.sketch_text.stroke-76"),sQuery(id+"F4.wireOp",EDGE,"E10.sketch_text.stroke-77"),sQuery(id+"F4.wireOp",EDGE,"E10.sketch_text.stroke-78"),sQuery(id+"F4.wireOp",EDGE,"E10.sketch_text.stroke-79"),sQuery(id+"F4.wireOp",EDGE,"E10.sketch_text.stroke-80"),sQuery(id+"F4.wireOp",EDGE,"E10.sketch_text.stroke-81"),sQuery(id+"F4.wireOp",EDGE,"E10.sketch_text.stroke-82"),sQuery(id+"F4.wireOp",EDGE,"E10.sketch_text.stroke-83"),sQuery(id+"F4.wireOp",EDGE,"E10.sketch_text.stroke-84"),sQuery(id+"F4.wireOp",EDGE,"E10.sketch_text.stroke-85"),sQuery(id+"F4.wireOp",EDGE,"E10.sketch_text.stroke-86"),sQuery(id+"F4.wireOp",EDGE,"E10.sketch_text.stroke-87"),sQuery(id+"F4.wireOp",EDGE,"E10.sketch_text.stroke-88"),sQuery(id+"F4.wireOp",EDGE,"E10.sketch_text.stroke-89"),sQuery(id+"F4.wireOp",EDGE,"E10.sketch_text.stroke-90"),sQuery(id+"F4.wireOp",EDGE,"E10.sketch_text.stroke-91"),sQuery(id+"F4.wireOp",EDGE,"E10.sketch_text.stroke-92"),sQuery(id+"F4.wireOp",EDGE,"E10.sketch_text.stroke-93"),sQuery(id+"F4.wireOp",EDGE,"E10.sketch_text.stroke-94"),sQuery(id+"F4.wireOp",EDGE,"E10.sketch_text.stroke-95"),sQuery(id+"F4.wireOp",EDGE,"E10.sketch_text.stroke-96"),sQuery(id+"F4.wireOp",EDGE,"E10.sketch_text.stroke-97"),sQuery(id+"F4.wireOp",EDGE,"E10.sketch_text.stroke-98"),sQuery(id+"F4.wireOp",EDGE,"E10.sketch_text.stroke-99"),sQuery(id+"F4.wireOp",EDGE,"E10.sketch_text.stroke-100"),sQuery(id+"F4.wireOp",EDGE,"E10.sketch_text.stroke-101"),sQuery(id+"F4.wireOp",EDGE,"E10.sketch_text.stroke-102"),sQuery(id+"F4.wireOp",EDGE,"E10.sketch_text.stroke-103"),sQuery(id+"F4.wireOp",EDGE,"E10.sketch_text.stroke-104")])],"isStart":false});
            var Q117;
            Q117=makeQuery(id+"F5.opExtrude","SWEPT_FACE",FACE,{"disambiguationData":[OSD([sQuery(id+"F4.wireOp",EDGE,"E10.sketch_text.stroke-33")])]});
            var Q118;
            Q118=makeQuery(id+"F5.opExtrude","SWEPT_FACE",FACE,{"disambiguationData":[OSD([sQuery(id+"F4.wireOp",EDGE,"E10.sketch_text.stroke-93")])]});
            var Q119;
            Q119=makeQuery(id+"F5.opExtrude","SWEPT_FACE",FACE,{"disambiguationData":[OSD([sQuery(id+"F4.wireOp",EDGE,"E10.sketch_text.stroke-34")])]});
            var Q120;
            Q120=makeQuery(id+"F5.opExtrude","SWEPT_FACE",FACE,{"disambiguationData":[OSD([sQuery(id+"F4.wireOp",EDGE,"E10.sketch_text.stroke-152")])]});
            var Q121;
            Q121=makeQuery(id+"F5.opExtrude","SWEPT_FACE",FACE,{"disambiguationData":[OSD([sQuery(id+"F4.wireOp",EDGE,"E10.sketch_text.stroke-51")])]});
            var Q122;
            Q122=makeQuery(id+"F5.opExtrude","SWEPT_FACE",FACE,{"disambiguationData":[OSD([sQuery(id+"F4.wireOp",EDGE,"E10.sketch_text.stroke-6")])]});
            var Q123;
            Q123=makeQuery(id+"F5.opExtrude","SWEPT_FACE",FACE,{"disambiguationData":[OSD([sQuery(id+"F4.wireOp",EDGE,"E10.sketch_text.stroke-7")])]});
            var Q124;
            Q124=makeQuery(id+"F5.opExtrude","SWEPT_FACE",FACE,{"disambiguationData":[OSD([sQuery(id+"F4.wireOp",EDGE,"E10.sketch_text.stroke-156")])]});
            var Q125;
            Q125=makeQuery(id+"F5.opExtrude","SWEPT_FACE",FACE,{"disambiguationData":[OSD([sQuery(id+"F4.wireOp",EDGE,"E10.sketch_text.stroke-112")])]});
            var Q126;
            Q126=makeQuery(id+"F5.boolean.opBoolean","SPLIT",FACE,{"disambiguationData":[TD([makeQuery(id+"F5.opExtrude","SWEPT_FACE",FACE,{"disambiguationData":[OSD([sQuery(id+"F4.wireOp",EDGE,"E10.sketch_text.stroke-182")])]})])],"derivedFrom":makeQuery(id+"F1.opExtrude","CAP_FACE",FACE,{"disambiguationData":[OSD([sQuery(id+"F0.wireOp",EDGE,"E0.bottom"),sQuery(id+"F0.wireOp",EDGE,"E0.top"),sQuery(id+"F0.wireOp",EDGE,"E0.left"),sQuery(id+"F0.wireOp",EDGE,"E0.right"),sQuery(id+"F0.wireOp",EDGE,"E1"),sQuery(id+"F0.wireOp",EDGE,"E7.MirrorC"),sQuery(id+"F0.wireOp",EDGE,"E8.MirrorC"),sQuery(id+"F0.wireOp",EDGE,"E9.MirrorC")])],"isStart":true})});
            var Q127;
            Q127=makeQuery(id+"F5.opExtrude","SWEPT_FACE",FACE,{"disambiguationData":[OSD([sQuery(id+"F4.wireOp",EDGE,"E10.sketch_text.stroke-96")])]});
            var Q128;
            Q128=makeQuery(id+"F5.opExtrude","SWEPT_FACE",FACE,{"disambiguationData":[OSD([sQuery(id+"F4.wireOp",EDGE,"E10.sketch_text.stroke-114")])]});
            var Q129;
            Q129=makeQuery(id+"F5.opExtrude","SWEPT_FACE",FACE,{"disambiguationData":[OSD([sQuery(id+"F4.wireOp",EDGE,"E10.sketch_text.stroke-39")])]});
            var Q130;
            Q130=makeQuery(id+"F5.opExtrude","SWEPT_FACE",FACE,{"disambiguationData":[OSD([sQuery(id+"F4.wireOp",EDGE,"E10.sketch_text.stroke-13")])]});
            var Q131;
            Q131=makeQuery(id+"F5.opExtrude","SWEPT_FACE",FACE,{"disambiguationData":[OSD([sQuery(id+"F4.wireOp",EDGE,"E10.sketch_text.stroke-115")])]});
            var Q132;
            Q132=makeQuery(id+"F5.opExtrude","SWEPT_FACE",FACE,{"disambiguationData":[OSD([sQuery(id+"F4.wireOp",EDGE,"E10.sketch_text.stroke-56")])]});
            var Q133;
            Q133=makeQuery(id+"F5.opExtrude","SWEPT_FACE",FACE,{"disambiguationData":[OSD([sQuery(id+"F4.wireOp",EDGE,"E10.sketch_text.stroke-144")])]});
            var Q134;
            Q134=makeQuery(id+"F5.opExtrude","SWEPT_FACE",FACE,{"disambiguationData":[OSD([sQuery(id+"F4.wireOp",EDGE,"E10.sketch_text.stroke-190")])]});
            var Q135;
            Q135=makeQuery(id+"F5.opExtrude","SWEPT_FACE",FACE,{"disambiguationData":[OSD([sQuery(id+"F4.wireOp",EDGE,"E10.sketch_text.stroke-116")])]});
            var Q136;
            Q136=makeQuery(id+"F5.opExtrude","SWEPT_FACE",FACE,{"disambiguationData":[OSD([sQuery(id+"F4.wireOp",EDGE,"E10.sketch_text.stroke-41")])]});
            var Q137;
            Q137=makeQuery(id+"F5.opExtrude","SWEPT_FACE",FACE,{"disambiguationData":[OSD([sQuery(id+"F4.wireOp",EDGE,"E10.sketch_text.stroke-161")])]});
            var Q138;
            Q138=makeQuery(id+"F5.opExtrude","SWEPT_FACE",FACE,{"disambiguationData":[OSD([sQuery(id+"F4.wireOp",EDGE,"E10.sketch_text.stroke-146")])]});
            var Q139;
            Q139=makeQuery(id+"F5.opExtrude","SWEPT_FACE",FACE,{"disambiguationData":[OSD([sQuery(id+"F4.wireOp",EDGE,"E10.sketch_text.stroke-58")])]});
            var Q140;
            Q140=makeQuery(id+"F5.opExtrude","SWEPT_FACE",FACE,{"disambiguationData":[OSD([sQuery(id+"F4.wireOp",EDGE,"E10.sketch_text.stroke-105")])]});
            var Q141;
            Q141=makeQuery(id+"F5.opExtrude","SWEPT_FACE",FACE,{"disambiguationData":[OSD([sQuery(id+"F4.wireOp",EDGE,"E10.sketch_text.stroke-177")])]});
            var Q142;
            Q142=makeQuery(id+"F5.opExtrude","SWEPT_FACE",FACE,{"disambiguationData":[OSD([sQuery(id+"F4.wireOp",EDGE,"E10.sketch_text.stroke-77")])]});
            var Q143;
            Q143=makeQuery(id+"F5.opExtrude","SWEPT_FACE",FACE,{"disambiguationData":[OSD([sQuery(id+"F4.wireOp",EDGE,"E10.sketch_text.stroke-138")])]});
            var Q144;
            Q144=makeQuery(id+"F5.opExtrude","SWEPT_FACE",FACE,{"disambiguationData":[OSD([sQuery(id+"F4.wireOp",EDGE,"E10.sketch_text.stroke-111")])]});
            var Q145;
            Q145=makeQuery(id+"F5.opExtrude","SWEPT_FACE",FACE,{"disambiguationData":[OSD([sQuery(id+"F4.wireOp",EDGE,"E10.sketch_text.stroke-53")])]});
            var Q146;
            Q146=makeQuery(id+"F5.opExtrude","SWEPT_FACE",FACE,{"disambiguationData":[OSD([sQuery(id+"F4.wireOp",EDGE,"E10.sketch_text.stroke-141")])]});
            var Q147;
            Q147=makeQuery(id+"F5.opExtrude","SWEPT_FACE",FACE,{"disambiguationData":[OSD([sQuery(id+"F4.wireOp",EDGE,"E10.sketch_text.stroke-157")])]});
            var Q148;
            Q148=makeQuery(id+"F5.opExtrude","SWEPT_FACE",FACE,{"disambiguationData":[OSD([sQuery(id+"F4.wireOp",EDGE,"E10.sketch_text.stroke-64")])]});
            var Q149;
            Q149=makeQuery(id+"F5.boolean.opBoolean","SPLIT",FACE,{"disambiguationData":[TD([makeQuery(id+"F5.opExtrude","SWEPT_FACE",FACE,{"disambiguationData":[OSD([sQuery(id+"F4.wireOp",EDGE,"E10.sketch_text.stroke-53")])]})])],"derivedFrom":makeQuery(id+"F1.opExtrude","CAP_FACE",FACE,{"disambiguationData":[OSD([sQuery(id+"F0.wireOp",EDGE,"E0.bottom"),sQuery(id+"F0.wireOp",EDGE,"E0.top"),sQuery(id+"F0.wireOp",EDGE,"E0.left"),sQuery(id+"F0.wireOp",EDGE,"E0.right"),sQuery(id+"F0.wireOp",EDGE,"E1"),sQuery(id+"F0.wireOp",EDGE,"E7.MirrorC"),sQuery(id+"F0.wireOp",EDGE,"E8.MirrorC"),sQuery(id+"F0.wireOp",EDGE,"E9.MirrorC")])],"isStart":true})});
            var Q150;
            Q150=makeQuery(id+"F5.opExtrude","SWEPT_FACE",FACE,{"disambiguationData":[OSD([sQuery(id+"F4.wireOp",EDGE,"E10.sketch_text.stroke-36")])]});
            var Q151;
            Q151=makeQuery(id+"F5.opExtrude","SWEPT_FACE",FACE,{"disambiguationData":[OSD([sQuery(id+"F4.wireOp",EDGE,"E10.sketch_text.stroke-22")])]});
            var Q152;
            Q152=makeQuery(id+"F5.boolean.opBoolean","SPLIT",FACE,{"disambiguationData":[TD([makeQuery(id+"F5.opExtrude","SWEPT_FACE",FACE,{"disambiguationData":[OSD([sQuery(id+"F4.wireOp",EDGE,"E10.sketch_text.stroke-119")])]})])],"derivedFrom":makeQuery(id+"F1.opExtrude","CAP_FACE",FACE,{"disambiguationData":[OSD([sQuery(id+"F0.wireOp",EDGE,"E0.bottom"),sQuery(id+"F0.wireOp",EDGE,"E0.top"),sQuery(id+"F0.wireOp",EDGE,"E0.left"),sQuery(id+"F0.wireOp",EDGE,"E0.right"),sQuery(id+"F0.wireOp",EDGE,"E1"),sQuery(id+"F0.wireOp",EDGE,"E7.MirrorC"),sQuery(id+"F0.wireOp",EDGE,"E8.MirrorC"),sQuery(id+"F0.wireOp",EDGE,"E9.MirrorC")])],"isStart":true})});
            var Q153;
            Q153=makeQuery(id+"F5.boolean.opBoolean","SPLIT",FACE,{"disambiguationData":[TD([makeQuery(id+"F5.opExtrude","SWEPT_FACE",FACE,{"disambiguationData":[OSD([sQuery(id+"F4.wireOp",EDGE,"E10.sketch_text.stroke-158")])]})])],"derivedFrom":makeQuery(id+"F1.opExtrude","CAP_FACE",FACE,{"disambiguationData":[OSD([sQuery(id+"F0.wireOp",EDGE,"E0.bottom"),sQuery(id+"F0.wireOp",EDGE,"E0.top"),sQuery(id+"F0.wireOp",EDGE,"E0.left"),sQuery(id+"F0.wireOp",EDGE,"E0.right"),sQuery(id+"F0.wireOp",EDGE,"E1"),sQuery(id+"F0.wireOp",EDGE,"E7.MirrorC"),sQuery(id+"F0.wireOp",EDGE,"E8.MirrorC"),sQuery(id+"F0.wireOp",EDGE,"E9.MirrorC")])],"isStart":true})});
            var Q154;
            Q154=makeQuery(id+"F5.opExtrude","SWEPT_FACE",FACE,{"disambiguationData":[OSD([sQuery(id+"F4.wireOp",EDGE,"E10.sketch_text.stroke-9")])]});
            var Q155;
            Q155=makeQuery(id+"F5.opExtrude","SWEPT_FACE",FACE,{"disambiguationData":[OSD([sQuery(id+"F4.wireOp",EDGE,"E10.sketch_text.stroke-167")])]});
            var Q156;
            Q156=makeQuery(id+"F5.opExtrude","SWEPT_FACE",FACE,{"disambiguationData":[OSD([sQuery(id+"F4.wireOp",EDGE,"E10.sketch_text.stroke-95")])]});
            var Q157;
            Q157=makeQuery(id+"F5.opExtrude","SWEPT_FACE",FACE,{"disambiguationData":[OSD([sQuery(id+"F4.wireOp",EDGE,"E10.sketch_text.stroke-184")])]});
            var Q158;
            Q158=makeQuery(id+"F5.opExtrude","SWEPT_FACE",FACE,{"disambiguationData":[OSD([sQuery(id+"F4.wireOp",EDGE,"E10.sketch_text.stroke-84")])]});
            var Q159;
            Q159=makeQuery(id+"F5.opExtrude","SWEPT_FACE",FACE,{"disambiguationData":[OSD([sQuery(id+"F4.wireOp",EDGE,"E10.sketch_text.stroke-68")])]});
            var Q160;
            Q160=makeQuery(id+"F5.opExtrude","SWEPT_FACE",FACE,{"disambiguationData":[OSD([sQuery(id+"F4.wireOp",EDGE,"E10.sketch_text.stroke-143")])]});
            var Q161;
            Q161=makeQuery(id+"F5.opExtrude","SWEPT_FACE",FACE,{"disambiguationData":[OSD([sQuery(id+"F4.wireOp",EDGE,"E10.sketch_text.stroke-189")])]});
            var Q162;
            Q162=makeQuery(id+"F5.opExtrude","CAP_FACE",FACE,{"disambiguationData":[OSD([sQuery(id+"F4.wireOp",EDGE,"E10.sketch_text.stroke-13"),sQuery(id+"F4.wireOp",EDGE,"E10.sketch_text.stroke-14"),sQuery(id+"F4.wireOp",EDGE,"E10.sketch_text.stroke-15"),sQuery(id+"F4.wireOp",EDGE,"E10.sketch_text.stroke-16"),sQuery(id+"F4.wireOp",EDGE,"E10.sketch_text.stroke-17"),sQuery(id+"F4.wireOp",EDGE,"E10.sketch_text.stroke-18"),sQuery(id+"F4.wireOp",EDGE,"E10.sketch_text.stroke-19"),sQuery(id+"F4.wireOp",EDGE,"E10.sketch_text.stroke-20")])],"isStart":false});
            var Q163;
            Q163=makeQuery(id+"F5.opExtrude","SWEPT_FACE",FACE,{"disambiguationData":[OSD([sQuery(id+"F4.wireOp",EDGE,"E10.sketch_text.stroke-57")])]});
            var Q164;
            Q164=makeQuery(id+"F5.opExtrude","SWEPT_FACE",FACE,{"disambiguationData":[OSD([sQuery(id+"F4.wireOp",EDGE,"E10.sketch_text.stroke-29")])]});
            var Q165;
            Q165=makeQuery(id+"F5.opExtrude","SWEPT_FACE",FACE,{"disambiguationData":[OSD([sQuery(id+"F4.wireOp",EDGE,"E10.sketch_text.stroke-60")])]});
            var Q166;
            Q166=makeQuery(id+"F5.opExtrude","SWEPT_FACE",FACE,{"disambiguationData":[OSD([sQuery(id+"F4.wireOp",EDGE,"E10.sketch_text.stroke-148")])]});
            var Q167;
            Q167=makeQuery(id+"F5.opExtrude","SWEPT_FACE",FACE,{"disambiguationData":[OSD([sQuery(id+"F4.wireOp",EDGE,"E10.sketch_text.stroke-75")])]});
            var Q168;
            Q168=makeQuery(id+"F5.opExtrude","SWEPT_FACE",FACE,{"disambiguationData":[OSD([sQuery(id+"F4.wireOp",EDGE,"E10.sketch_text.stroke-91")])]});
            var Q169;
            Q169=makeQuery(id+"F5.opExtrude","SWEPT_FACE",FACE,{"disambiguationData":[OSD([sQuery(id+"F4.wireOp",EDGE,"E10.sketch_text.stroke-78")])]});
            var Q170;
            Q170=makeQuery(id+"F5.opExtrude","SWEPT_FACE",FACE,{"disambiguationData":[OSD([sQuery(id+"F4.wireOp",EDGE,"E10.sketch_text.stroke-62")])]});
            var Q171;
            Q171=makeQuery(id+"F5.opExtrude","SWEPT_FACE",FACE,{"disambiguationData":[OSD([sQuery(id+"F4.wireOp",EDGE,"E10.sketch_text.stroke-182")])]});
            var Q172;
            Q172=makeQuery(id+"F5.opExtrude","SWEPT_FACE",FACE,{"disambiguationData":[OSD([sQuery(id+"F4.wireOp",EDGE,"E10.sketch_text.stroke-11")])]});
            var Q173;
            Q173=makeQuery(id+"F5.opExtrude","SWEPT_FACE",FACE,{"disambiguationData":[OSD([sQuery(id+"F4.wireOp",EDGE,"E10.sketch_text.stroke-97")])]});
            var Q174;
            Q174=makeQuery(id+"F5.opExtrude","SWEPT_FACE",FACE,{"disambiguationData":[OSD([sQuery(id+"F4.wireOp",EDGE,"E10.sketch_text.stroke-23")])]});
            var Q175;
            Q175=makeQuery(id+"F5.opExtrude","SWEPT_FACE",FACE,{"disambiguationData":[OSD([sQuery(id+"F4.wireOp",EDGE,"E10.sketch_text.stroke-80")])]});
            var Q176;
            Q176=makeQuery(id+"F5.boolean.opBoolean","SPLIT",FACE,{"disambiguationData":[TD([makeQuery(id+"F5.opExtrude","SWEPT_FACE",FACE,{"disambiguationData":[OSD([sQuery(id+"F4.wireOp",EDGE,"E10.sketch_text.stroke-99")])]})])],"derivedFrom":makeQuery(id+"F1.opExtrude","CAP_FACE",FACE,{"disambiguationData":[OSD([sQuery(id+"F0.wireOp",EDGE,"E0.bottom"),sQuery(id+"F0.wireOp",EDGE,"E0.top"),sQuery(id+"F0.wireOp",EDGE,"E0.left"),sQuery(id+"F0.wireOp",EDGE,"E0.right"),sQuery(id+"F0.wireOp",EDGE,"E1"),sQuery(id+"F0.wireOp",EDGE,"E7.MirrorC"),sQuery(id+"F0.wireOp",EDGE,"E8.MirrorC"),sQuery(id+"F0.wireOp",EDGE,"E9.MirrorC")])],"isStart":true})});
            var Q177;
            Q177=makeQuery(id+"F5.opExtrude","SWEPT_FACE",FACE,{"disambiguationData":[OSD([sQuery(id+"F4.wireOp",EDGE,"E10.sketch_text.stroke-168")])]});
            var Q178;
            Q178=makeQuery(id+"F5.opExtrude","SWEPT_FACE",FACE,{"disambiguationData":[OSD([sQuery(id+"F4.wireOp",EDGE,"E10.sketch_text.stroke-188")])]});
            var Q179;
            Q179=makeQuery(id+"F5.opExtrude","SWEPT_FACE",FACE,{"disambiguationData":[OSD([sQuery(id+"F4.wireOp",EDGE,"E10.sketch_text.stroke-129")])]});
            var Q180;
            Q180=makeQuery(id+"F5.opExtrude","SWEPT_FACE",FACE,{"disambiguationData":[OSD([sQuery(id+"F4.wireOp",EDGE,"E10.sketch_text.stroke-27")])]});
            var Q181;
            Q181=makeQuery(id+"F5.opExtrude","SWEPT_FACE",FACE,{"disambiguationData":[OSD([sQuery(id+"F4.wireOp",EDGE,"E10.sketch_text.stroke-175")])]});
            var Q182;
            Q182=makeQuery(id+"F5.opExtrude","SWEPT_FACE",FACE,{"disambiguationData":[OSD([sQuery(id+"F4.wireOp",EDGE,"E10.sketch_text.stroke-42")])]});
            var Q183;
            Q183=makeQuery(id+"F5.opExtrude","SWEPT_FACE",FACE,{"disambiguationData":[OSD([sQuery(id+"F4.wireOp",EDGE,"E10.sketch_text.stroke-118")])]});
            var Q184;
            Q184=makeQuery(id+"F5.opExtrude","SWEPT_FACE",FACE,{"disambiguationData":[OSD([sQuery(id+"F4.wireOp",EDGE,"E10.sketch_text.stroke-151")])]});
            var Q185;
            Q185=makeQuery(id+"F5.opExtrude","SWEPT_FACE",FACE,{"disambiguationData":[OSD([sQuery(id+"F4.wireOp",EDGE,"E10.sketch_text.stroke-137")])]});
            var Q186;
            Q186=makeQuery(id+"F5.opExtrude","SWEPT_FACE",FACE,{"disambiguationData":[OSD([sQuery(id+"F4.wireOp",EDGE,"E10.sketch_text.stroke-83")])]});
            var Q187;
            Q187=makeQuery(id+"F5.boolean.opBoolean","SPLIT",FACE,{"disambiguationData":[TD([makeQuery(id+"F5.opExtrude","SWEPT_FACE",FACE,{"disambiguationData":[OSD([sQuery(id+"F4.wireOp",EDGE,"E10.sketch_text.stroke-90")])]})])],"derivedFrom":makeQuery(id+"F1.opExtrude","CAP_FACE",FACE,{"disambiguationData":[OSD([sQuery(id+"F0.wireOp",EDGE,"E0.bottom"),sQuery(id+"F0.wireOp",EDGE,"E0.top"),sQuery(id+"F0.wireOp",EDGE,"E0.left"),sQuery(id+"F0.wireOp",EDGE,"E0.right"),sQuery(id+"F0.wireOp",EDGE,"E1"),sQuery(id+"F0.wireOp",EDGE,"E7.MirrorC"),sQuery(id+"F0.wireOp",EDGE,"E8.MirrorC"),sQuery(id+"F0.wireOp",EDGE,"E9.MirrorC")])],"isStart":true})});
            var Q188;
            Q188=makeQuery(id+"F5.opExtrude","SWEPT_FACE",FACE,{"disambiguationData":[OSD([sQuery(id+"F4.wireOp",EDGE,"E10.sketch_text.stroke-139")])]});
            var Q189;
            Q189=makeQuery(id+"F5.opExtrude","SWEPT_FACE",FACE,{"disambiguationData":[OSD([sQuery(id+"F4.wireOp",EDGE,"E10.sketch_text.stroke-70")])]});
            var Q190;
            Q190=makeQuery(id+"F5.opExtrude","SWEPT_FACE",FACE,{"disambiguationData":[OSD([sQuery(id+"F4.wireOp",EDGE,"E10.sketch_text.stroke-160")])]});
            var Q191;
            Q191=makeQuery(id+"F5.opExtrude","SWEPT_FACE",FACE,{"disambiguationData":[OSD([sQuery(id+"F4.wireOp",EDGE,"E10.sketch_text.stroke-71")])]});
            var Q192;
            Q192=makeQuery(id+"F5.opExtrude","SWEPT_FACE",FACE,{"disambiguationData":[OSD([sQuery(id+"F4.wireOp",EDGE,"E10.sketch_text.stroke-117")])]});
            var Q193;
            Q193=makeQuery(id+"F5.opExtrude","SWEPT_FACE",FACE,{"disambiguationData":[OSD([sQuery(id+"F4.wireOp",EDGE,"E10.sketch_text.stroke-147")])]});
            var Q194;
            Q194=makeQuery(id+"F5.opExtrude","SWEPT_FACE",FACE,{"disambiguationData":[OSD([sQuery(id+"F4.wireOp",EDGE,"E10.sketch_text.stroke-164")])]});
            var Q195;
            Q195=makeQuery(id+"F5.opExtrude","SWEPT_FACE",FACE,{"disambiguationData":[OSD([sQuery(id+"F4.wireOp",EDGE,"E10.sketch_text.stroke-61")])]});
            var Q196;
            Q196=makeQuery(id+"F5.opExtrude","SWEPT_FACE",FACE,{"disambiguationData":[OSD([sQuery(id+"F4.wireOp",EDGE,"E10.sketch_text.stroke-19")])]});
            var Q197;
            Q197=makeQuery(id+"F5.opExtrude","SWEPT_FACE",FACE,{"disambiguationData":[OSD([sQuery(id+"F4.wireOp",EDGE,"E10.sketch_text.stroke-35")])]});
            var Q198;
            Q198=makeQuery(id+"F5.opExtrude","SWEPT_FACE",FACE,{"disambiguationData":[OSD([sQuery(id+"F4.wireOp",EDGE,"E10.sketch_text.stroke-140")])]});
            var Q199;
            Q199=makeQuery(id+"F5.opExtrude","SWEPT_FACE",FACE,{"disambiguationData":[OSD([sQuery(id+"F4.wireOp",EDGE,"E10.sketch_text.stroke-20")])]});
            var Q200;
            Q200=makeQuery(id+"F5.opExtrude","SWEPT_FACE",FACE,{"disambiguationData":[OSD([sQuery(id+"F4.wireOp",EDGE,"E10.sketch_text.stroke-16")])]});
            var Q201;
            Q201=makeQuery(id+"F5.opExtrude","SWEPT_FACE",FACE,{"disambiguationData":[OSD([sQuery(id+"F4.wireOp",EDGE,"E10.sketch_text.stroke-18")])]});
            var Q202;
            Q202=makeQuery(id+"F5.opExtrude","SWEPT_FACE",FACE,{"disambiguationData":[OSD([sQuery(id+"F4.wireOp",EDGE,"E10.sketch_text.stroke-17")])]});
            var Q203;
            Q203=qCreatedBy(makeId("Right.planeOp"),FACE);
            mirror(context, id + "F6", {"operationType" : NewBodyOperationType.ADD, "entities" : qUnion([Q0]), "faces" : qUnion([Q1, Q2, Q3, Q4, Q5, Q6, Q7, Q8, Q9, Q10, Q11, Q12, Q13, Q14, Q15, Q16, Q17, Q18, Q19, Q20, Q21, Q22, Q23, Q24, Q25, Q26, Q27, Q28, Q29, Q30, Q31, Q32, Q33, Q34, Q35, Q36, Q37, Q38, Q39, Q40, Q41, Q42, Q43, Q44, Q45, Q46, Q47, Q48, Q49, Q50, Q51, Q52, Q53, Q54, Q55, Q56, Q57, Q58, Q59, Q60, Q61, Q62, Q63, Q64, Q65, Q66, Q67, Q68, Q69, Q70, Q71, Q72, Q73, Q74, Q75, Q76, Q77, Q78, Q79, Q80, Q81, Q82, Q83, Q84, Q85, Q86, Q87, Q88, Q89, Q90, Q91, Q92, Q93, Q94, Q95, Q96, Q97, Q98, Q99, Q100, Q101, Q102, Q103, Q104, Q105, Q106, Q107, Q108, Q109, Q110, Q111, Q112, Q113, Q114, Q115, Q116, Q117, Q118, Q119, Q120, Q121, Q122, Q123, Q124, Q125, Q126, Q127, Q128, Q129, Q130, Q131, Q132, Q133, Q134, Q135, Q136, Q137, Q138, Q139, Q140, Q141, Q142, Q143, Q144, Q145, Q146, Q147, Q148, Q149, Q150, Q151, Q152, Q153, Q154, Q155, Q156, Q157, Q158, Q159, Q160, Q161, Q162, Q163, Q164, Q165, Q166, Q167, Q168, Q169, Q170, Q171, Q172, Q173, Q174, Q175, Q176, Q177, Q178, Q179, Q180, Q181, Q182, Q183, Q184, Q185, Q186, Q187, Q188, Q189, Q190, Q191, Q192, Q193, Q194, Q195, Q196, Q197, Q198, Q199, Q200, Q201, Q202]), "mirrorPlane" : qUnion([Q203])});
        }
    });
